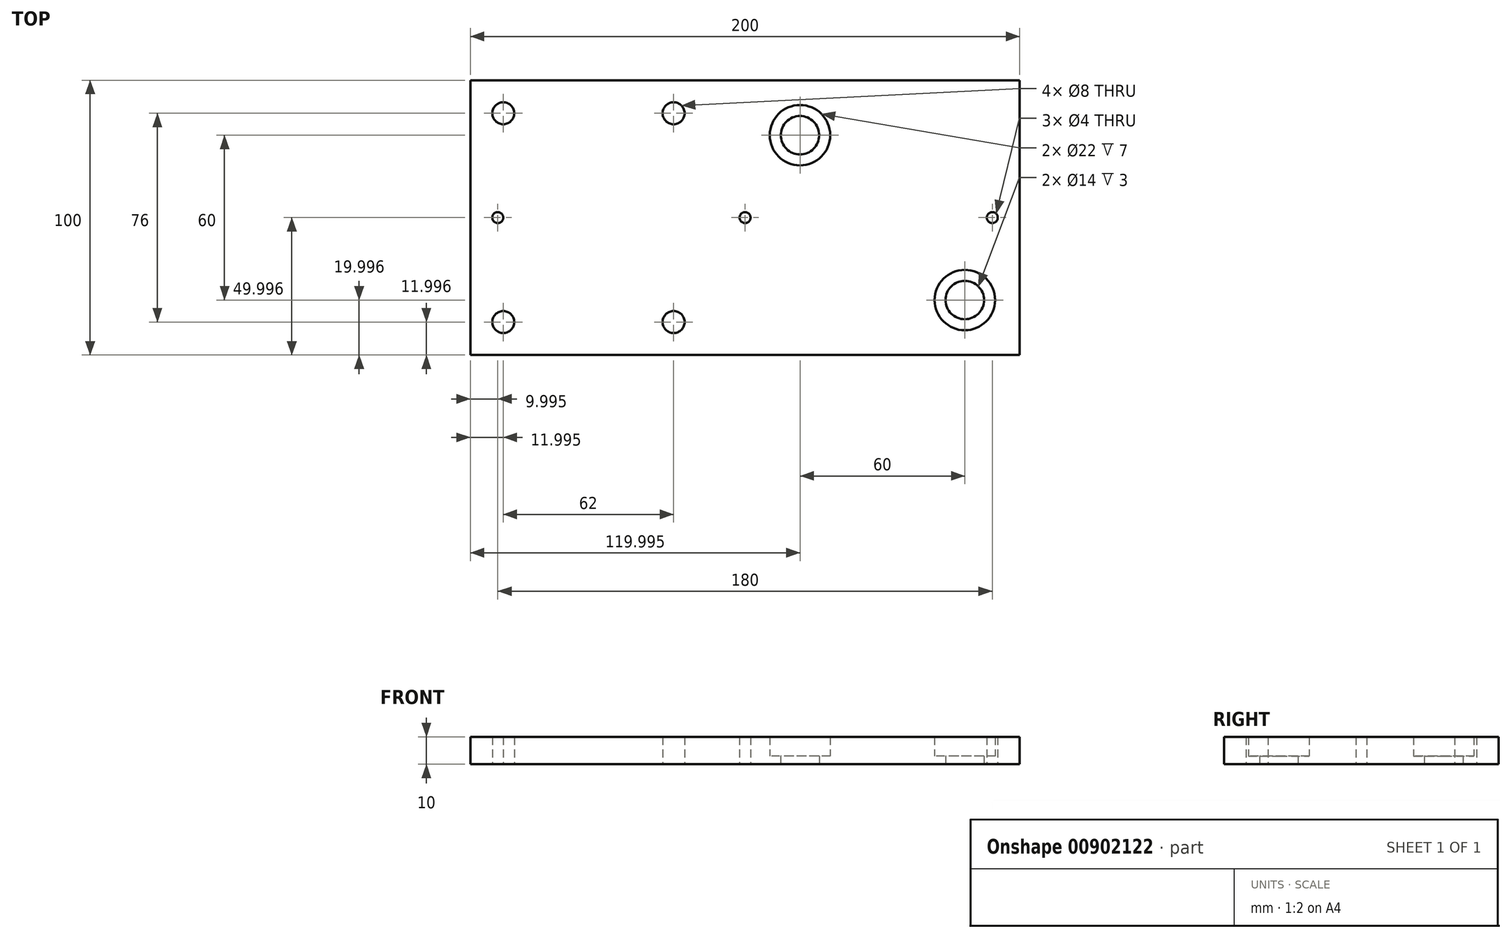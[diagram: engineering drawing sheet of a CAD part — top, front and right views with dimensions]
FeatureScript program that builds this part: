
annotation { "Feature Type Name" : "Feature", "Feature Type Description" : "" }
export const myFeature = defineFeature(function(context is Context, id is Id, definition is map)
    precondition{}
    {
        {
            var Q0;
            Q0=qCreatedBy(makeId("Top.planeOp"),FACE);
            var sketch = newSketch(context, id + "F0", { "sketchPlane" : qUnion([Q0])});
            skLineSegment(sketch, "E0.bottom", {"start": v(-136.01, 62.84) * mm, "end": v(63.99, 62.84) * mm});
            skLineSegment(sketch, "E0.top", {"start": v(-136.01, -37.16) * mm, "end": v(63.99, -37.16) * mm});
            skLineSegment(sketch, "E0.left", {"start": v(-136.01, 62.84) * mm, "end": v(-136.01, -37.16) * mm});
            skLineSegment(sketch, "E0.right", {"start": v(63.99, 62.84) * mm, "end": v(63.99, -37.16) * mm});
            skCircle(sketch, "E1", {"center": v(-124.01, 50.84) * mm, "radius": 4 * mm});
            skCircle(sketch, "E2.MirrorC", {"center": v(-124, -25.16) * mm, "radius": 4 * mm});
            skCircle(sketch, "E3.MirrorC", {"center": v(-62.01, 50.84) * mm, "radius": 4 * mm});
            skCircle(sketch, "E4.MirrorC", {"center": v(-62.01, -25.16) * mm, "radius": 4 * mm});
            skCircle(sketch, "E5", {"center": v(-126.01, 12.84) * mm, "radius": 2 * mm});
            skCircle(sketch, "E6", {"center": v(-36.01, 12.84) * mm, "radius": 2 * mm});
            skCircle(sketch, "E7", {"center": v(53.99, 12.84) * mm, "radius": 2 * mm});
            skLineSegment(sketch, "E8", {"start": v(63.99, -37.16) * mm, "end": v(43.99, -37.16) * mm});
            skLineSegment(sketch, "E9", {"start": v(43.99, -37.16) * mm, "end": v(43.99, -17.16) * mm});
            skCircle(sketch, "E10", {"center": v(-16.01, 42.84) * mm, "radius": 7 * mm});
            skCircle(sketch, "E11", {"center": v(-16.01, 42.84) * mm, "radius": 11 * mm});
            skCircle(sketch, "E12", {"center": v(43.99, -17.16) * mm, "radius": 7 * mm});
            skCircle(sketch, "E13", {"center": v(43.99, -17.16) * mm, "radius": 11 * mm});
            skSolve(sketch);
        }
        {
            var Q0;
            Q0=makeQuery(id+"F0.imprint","IMPRINT",FACE,{"disambiguationData":[TD([[makeQuery(id+"F0.imprint","IMPRINT",EDGE,{"derivedFrom":sQuery(id+"F0.wireOp",EDGE,"E0.bottom")}),-1.0]])]});
            extrude(context, id + "F1", {"entities" : qUnion([Q0]), "depth" : 10 * mm, "offsetDistance" : 25 * mm});
        }
        {
            var Q0;
            Q0=makeQuery(id+"F0.imprint","IMPRINT",FACE,{"disambiguationData":[TD([[makeQuery(id+"F0.imprint","IMPRINT",EDGE,{"derivedFrom":sQuery(id+"F0.wireOp",EDGE,"E10")}),-1.0]])]});
            var Q1;
            Q1=makeQuery(id+"F0.imprint","IMPRINT",FACE,{"disambiguationData":[TD([[makeQuery(id+"F0.imprint","IMPRINT",EDGE,{"derivedFrom":sQuery(id+"F0.wireOp",EDGE,"E12")}),-1.0]])]});
            extrude(context, id + "F2", {"entities" : qUnion([Q0, Q1]), "operationType" : NewBodyOperationType.ADD, "depth" : 3 * mm, "offsetDistance" : 25 * mm});
        }
    });
